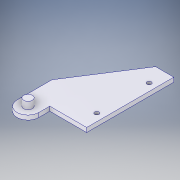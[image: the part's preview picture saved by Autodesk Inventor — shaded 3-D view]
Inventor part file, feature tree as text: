
AUTODESK INVENTOR PART (.ipt)
format: ipt  version: 2017 (Build 210142000, 142)  size: 122,880 bytes
history: native  units: in
note: dims shown in document units (in); Inventor stores cm internally (conversion verified against a paired STEP export)
features: extrude x2, sketch x2
ambient origin geometry x8: Origin, YZ Plane, XZ Plane, XY Plane, X Axis, Y Axis, Z Axis, Center Point
bodies: Solid1 (feature_tree)
feature tree (4):
  extrude  "Extrusion1"  TaperAngle=90.0deg  [1 undecoded]
  extrude  "Extrusion2"  Depth=1.0in
  sketch  "Sketch3"  dims[d6=2.3622in d7=90.0deg]
  sketch  "Sketch4"  dims[d8=0.4929in d9=1.0in d10=0.2953in d11=0.5906in d12=0.2362in d13=0.9456in d14=0.1181in d15=0.0in d16=0.315in d17=0.0in d18=0.1969in d19=0.4724in d20=0.4724in d21=0.1181in d22=0.1181in]
note: 1 required parameter value undecoded (feature->parameter linkage not recoverable at this tier; creation-order binding heuristic only, values carry confidence <= 0.55)
